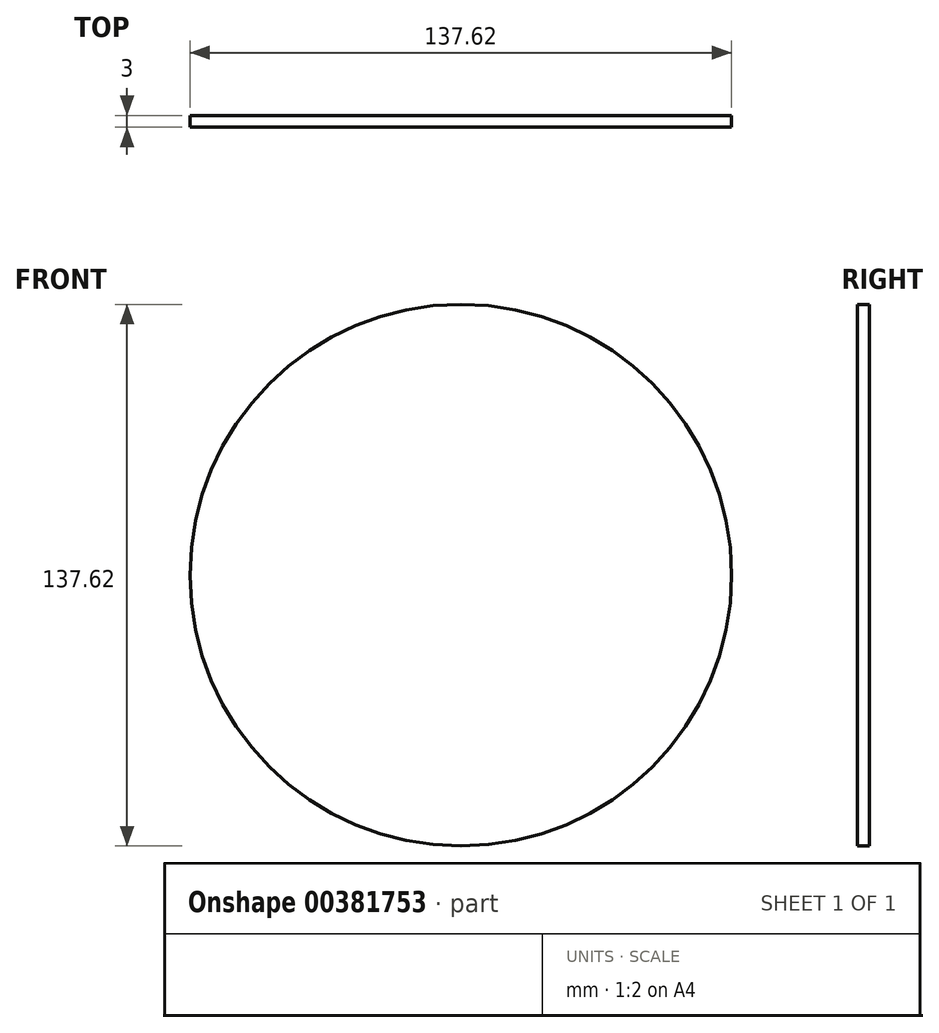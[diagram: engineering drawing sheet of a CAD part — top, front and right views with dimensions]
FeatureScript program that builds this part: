
annotation { "Feature Type Name" : "Feature", "Feature Type Description" : "" }
export const myFeature = defineFeature(function(context is Context, id is Id, definition is map)
    precondition{}
    {
        {
            var Q0;
            Q0=qCreatedBy(makeId("Front.planeOp"),FACE);
            var sketch = newSketch(context, id + "F0", { "sketchPlane" : qUnion([Q0])});
            skCircle(sketch, "E0", {"center": v(0, 0) * mm, "radius": 68.8 * mm});
            skCircle(sketch, "E1", {"center": v(0, 0) * mm, "radius": 4.5 * mm});
            skSolve(sketch);
        }
        {
            var Q0;
            Q0=sQuery(id+"F0.wireOp",EDGE,"E0");
            extrude(context, id + "F1", {"bodyType" : ToolBodyType.SURFACE, "surfaceEntities" : qUnion([Q0]), "depth" : 3 * mm});
        }
    });
